# Revit family: Ellipse – Free Standing
name_source: partatom
category: Furniture
units: mm (PartAtom-declared; Revit-internal decimal feet)

## family parameters
Always vertical = Yes
Cut with Voids When Loaded = No
OmniClass Number = 23.21.23.13.15
Room Calculation Point = No
Shared = No
Work Plane-Based = No

## types (2) — shared parameters
Construction Anchoring Material = Concrete, Cast-in-Place - C10
Construction material = Hags - Steel - Galvanized
Edition number = 1
IFC Classification = Furniture
Manufacturer = Hags
Manufacturer name = HAGS
OmniClass Code = 23-21 23 13 15
Product Guid = 90e49432-c870-4a59-897e-b15016e8f9bd
Product data url = https://bimobject.com
Product url = https://hags.se
QR code = https://www.hags.com
URL = https://www.hags.com
Uniclass 1.4 Code = L8211
Uniclass 1.4 Description = Furniture
zero-valued in all types: Default Elevation

## per-type parameters (varying)
| type | BIMobject category | Body material | Body material_90 | Description | Model | OmniClass Description | Product SKU | Product name |
| 8000135 / Ellipse - Freestanding | LItter Bins | Plastic Black | Plastic Black |  | 8000135 | Residential Litter Bins | Ellipse_Detached | Ellipse - Freestanding |
| 8037716 / Galvanized | Bench & Park Bench | Hags - Steel - Galvanized | Hags - Steel - Galvanized | Sofa Sofiero Detached | 8037014 | Residential Sofas | Table_Ekeby_Detached | Ekeby Table Cast In Place |

## geometry (parser evidence)
native form markers: Sweep x2
no freeform markers — native parametric forms only
